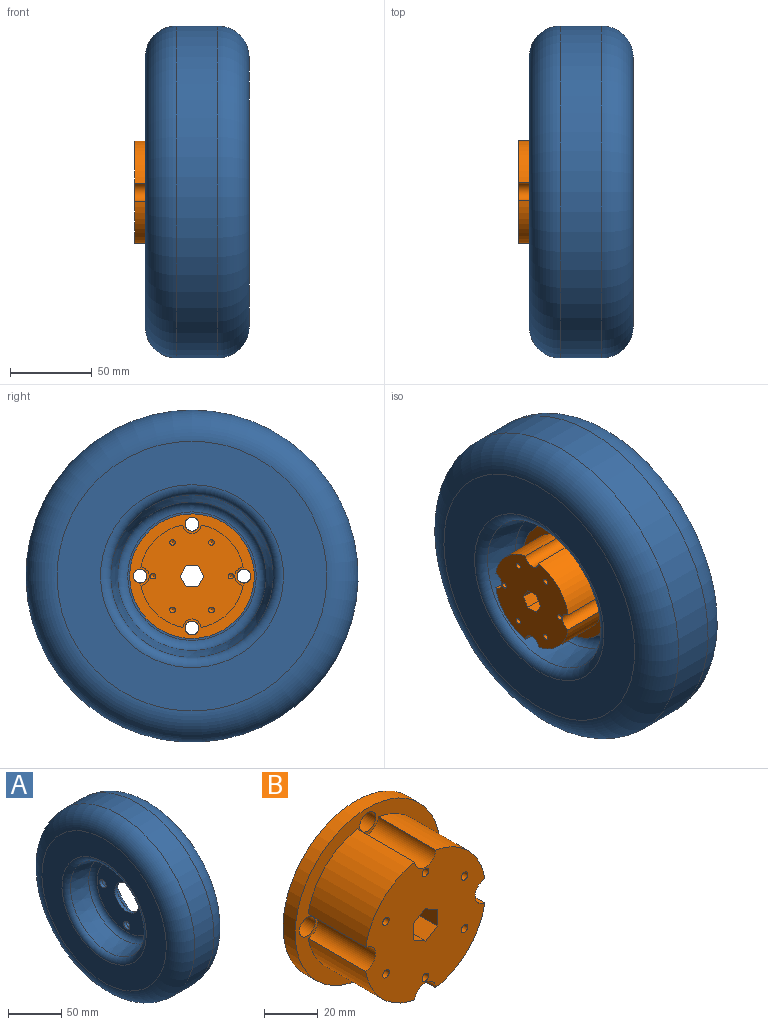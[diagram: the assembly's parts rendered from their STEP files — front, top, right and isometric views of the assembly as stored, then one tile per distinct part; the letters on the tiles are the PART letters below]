
ASSEMBLY  parts=2 mates=1
PART A: 18 faces, bbox 63.5x219.9x219.9 mm
  f0: torus R=82.55mm, axis (-1,0,0), area 17800.9mm2, adj f1,f12
  f1: plane 165.1x165.1mm, normal (-1,0,0), area 11573.1mm2, adj f0,f2
  f2: torus R=55.95mm, axis (-1,0,0), area 2842.3mm2, adj f1,f3
  f3: cone r=49.74mm half-angle=11.9deg, axis (-1,0,0), area 6140mm2, adj f2,f4
  f4: torus R=39.3mm, axis (-1,0,0), area 2338.7mm2, adj f3,f5
  f5: plane 78.6x78.6mm, normal (-1,0,0), area 3836.4mm2, adj f4,f13,f14,f15,f16,f17
  f6: plane 78.6x78.6mm, normal (1,0,0), area 3836.4mm2, adj f7,f13,f14,f15,f16,f17
  f7: torus R=39.3mm, axis (-1,0,0), area 2338.7mm2, adj f6,f8
  f8: cone r=45.51mm half-angle=11.9deg, axis (1,0,0), area 6140mm2, adj f7,f9
  f9: torus R=55.95mm, axis (-1,0,0), area 2842.3mm2, adj f8,f10
  f10: plane 165.1x165.1mm, normal (1,0,0), area 11573.1mm2, adj f9,f11
  f11: torus R=82.55mm, axis (-1,0,0), area 17800.9mm2, adj f10,f12
  f12: cylinder r=101.6mm len=203.2mm, axis (-1,0,0), area 16214.6mm2, adj f0,f11
  f13: cylinder r=15.88mm len=31.75mm, axis (-1,0,0), area 316.7mm2, adj f5,f6
  f14: cylinder r=4.22mm len=8.43mm, axis (-1,0,0), area 84.1mm2, adj f5,f6
  f15: cylinder r=4.22mm len=8.43mm, axis (-1,0,0), area 84.1mm2, adj f5,f6
  f16: cylinder r=4.22mm len=8.43mm, axis (-1,0,0), area 84.1mm2, adj f5,f6
  f17: cylinder r=4.22mm len=8.43mm, axis (-1,0,0), area 84.1mm2, adj f5,f6
PART B: 36 faces, bbox 76.2x49.2x76.2 mm
  f0: plane 76.2x76.2mm, normal (0,-1,0), area 1356.8mm2, adj f1,f3,f4,f5,f6,f7,f8,f9
  f1: cylinder r=38.1mm len=76.2mm, axis (0,1,0), area 1520.1mm2, adj f0,f2
  f2: plane 76.2x76.2mm, normal (0,1,0), area 3545.2mm2, adj f1,f12,f20,f21,f22,f23
  f3: cylinder r=5.56mm len=30.16mm, axis (0,1,0), area 497.1mm2, adj f0,f4,f10,f11
  f4: cylinder r=31.75mm len=30.16mm, axis (0,1,0), area 1168.7mm2, adj f0,f3,f5,f11
  f5: cylinder r=5.56mm len=30.16mm, axis (0,1,0), area 497.1mm2, adj f0,f4,f6,f11
  f6: cylinder r=31.75mm len=30.16mm, axis (0,1,0), area 1168.7mm2, adj f0,f5,f7,f11
  f7: cylinder r=5.56mm len=30.16mm, axis (0,1,0), area 497.1mm2, adj f0,f6,f8,f11
  f8: cylinder r=31.75mm len=30.16mm, axis (0,1,0), area 1168.7mm2, adj f0,f7,f9,f11
  f9: cylinder r=5.56mm len=30.16mm, axis (0,1,0), area 497.1mm2, adj f0,f8,f10,f11
  f10: cylinder r=31.75mm len=30.16mm, axis (0,1,0), area 1168.7mm2, adj f0,f3,f9,f11
  f11: plane 62.53x62.53mm, normal (0,-1,0), area 2784.2mm2, adj f3,f4,f5,f6,f7,f8,f9,f10
  f12: cylinder r=15.88mm len=31.75mm, axis (0,-1,0), area 1266.8mm2, adj f2,f13
  f13: plane 31.75x31.75mm, normal (0,1,0), area 652mm2, adj f12,f14,f15,f16,f17,f18,f19
  f14: plane 49.21x6.35mm, normal (-0.5,0,0.87), area 360.8mm2, adj f11,f13,f15,f19
  f15: plane 49.21x7.33mm, normal (-1,0,0), area 360.8mm2, adj f11,f13,f14,f16
  f16: plane 49.21x6.35mm, normal (-0.5,0,-0.87), area 360.8mm2, adj f11,f13,f15,f17
  f17: plane 49.21x6.35mm, normal (0.5,0,-0.87), area 360.8mm2, adj f11,f13,f16,f18
  f18: plane 49.21x7.33mm, normal (1,0,0), area 360.8mm2, adj f11,f13,f17,f19
  f19: plane 49.21x6.35mm, normal (0.5,0,0.87), area 360.8mm2, adj f11,f13,f14,f18
  f20: cylinder r=4.22mm len=8.43mm, axis (0,-1,0), area 168.2mm2, adj f0,f2
  f21: cylinder r=4.22mm len=8.43mm, axis (0,-1,0), area 168.2mm2, adj f0,f2
  f22: cylinder r=4.22mm len=8.43mm, axis (0,-1,0), area 168.2mm2, adj f0,f2
  f23: cylinder r=4.22mm len=8.43mm, axis (0,-1,0), area 168.2mm2, adj f0,f2
  f24: cone r=0mm half-angle=59deg, axis (0,-1,0), area 10.9mm2, adj f25
  f25: cylinder r=1.73mm len=21.43mm, axis (0,-1,0), area 232.6mm2, adj f11,f24
  f26: cone r=0mm half-angle=59deg, axis (0,-1,0), area 10.9mm2, adj f27
  f27: cylinder r=1.73mm len=21.43mm, axis (0,-1,0), area 232.6mm2, adj f11,f26
  f28: cone r=0mm half-angle=59deg, axis (0,-1,0), area 10.9mm2, adj f29
  f29: cylinder r=1.73mm len=21.43mm, axis (0,-1,0), area 232.6mm2, adj f11,f28
  f30: cone r=0mm half-angle=59deg, axis (0,-1,0), area 10.9mm2, adj f31
  f31: cylinder r=1.73mm len=21.43mm, axis (0,-1,0), area 232.6mm2, adj f11,f30
  f32: cone r=0mm half-angle=59deg, axis (0,-1,0), area 10.9mm2, adj f33
  f33: cylinder r=1.73mm len=21.43mm, axis (0,-1,0), area 232.6mm2, adj f11,f32
  f34: cone r=0mm half-angle=59deg, axis (0,-1,0), area 10.9mm2, adj f35
  f35: cylinder r=1.73mm len=21.43mm, axis (0,-1,0), area 232.6mm2, adj f11,f34
PLACE A at identity fixed
PLACE B rot(axis=(0.58,0.58,-0.58),120deg) t=(-1.59,0,0)mm
MATE fastened A.f15 <-> B.f23  axis (-1,0,0) through (-1.59,-31.75,0)mm
